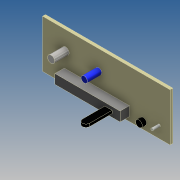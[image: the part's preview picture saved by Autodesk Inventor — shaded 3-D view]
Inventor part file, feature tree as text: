
AUTODESK INVENTOR PART (.ipt)
format: ipt  version: 2016 (Build 200138000, 138)  size: 124,928 bytes
history: native  units: mm
features: extrude x7, sketch x4, fillet x1
ambient origin geometry x8: Origin, YZ Plane, XZ Plane, XY Plane, X Axis, Y Axis, Z Axis, Center Point
bodies: Solid1 (feature_tree)
feature tree (12):
  extrude  "Extrusion1"  Depth=88.0mm
  extrude  "Extrusion2"  Depth=15.0mm
  extrude  "Extrusion3"  Depth=45.0mm
  fillet  "Fillet1"  Radius=3.0mm
  sketch  "Sketch4"  dims[d8=6.5mm d9=0.0mm d10=34.5mm d11=5.0mm d12=2.0mm d13=18.0mm d14=0.0mm d15=10.0mm d16=0.0mm d17=10.0mm d18=0.0mm d19=3.0mm d20=0.0mm d21=5.0mm d22=0.0mm]
  extrude  "Extrusion4"  Depth=34.5mm
  extrude  "Extrusion5"  Depth=5.0mm
  extrude  "Extrusion6"  Depth=2.0mm
  extrude  "Extrusion7"  Depth=5.0mm TaperAngle=0.0deg
  sketch  "Sketch1"  dims[d0=33.0mm d1=88.0mm]
  sketch  "Sketch2"  dims[d2=2.0mm d3=0.0mm d4=15.0mm]
  sketch  "Sketch3"  dims[d5=9.5mm d6=45.0mm d7=3.0mm]
